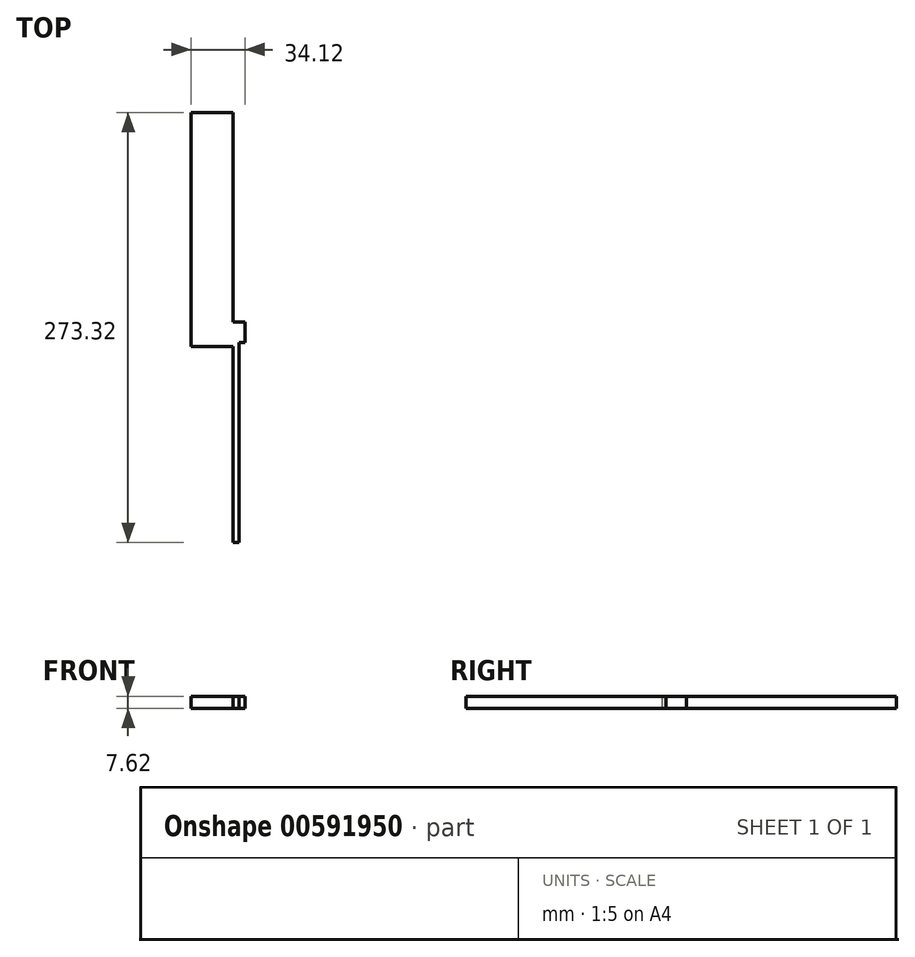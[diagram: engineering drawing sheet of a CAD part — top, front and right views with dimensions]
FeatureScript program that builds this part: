
annotation { "Feature Type Name" : "Feature", "Feature Type Description" : "" }
export const myFeature = defineFeature(function(context is Context, id is Id, definition is map)
    precondition{}
    {
        {
            var Q0;
            Q0=qCreatedBy(makeId("Top.planeOp"),FACE);
            var sketch = newSketch(context, id + "F0", { "sketchPlane" : qUnion([Q0])});
            skLineSegment(sketch, "E0.bottom", {"start": v(-51.2, 33.08) * mm, "end": v(-24.7, 33.08) * mm});
            skLineSegment(sketch, "E0.top", {"start": v(-51.2, -115.79) * mm, "end": v(-24.7, -115.79) * mm});
            skLineSegment(sketch, "E0.left", {"start": v(-51.2, 33.08) * mm, "end": v(-51.2, -115.79) * mm});
            skLineSegment(sketch, "E0.right", {"start": v(-24.7, 33.08) * mm, "end": v(-24.7, -115.79) * mm});
            skSolve(sketch);
        }
        {
            var Q0;
            Q0=makeQuery(id+"F0.imprint","IMPRINT",FACE,{"disambiguationData":[TD([[makeQuery(id+"F0.imprint","IMPRINT",EDGE,{"derivedFrom":sQuery(id+"F0.wireOp",EDGE,"E0.bottom")}),-1.0]])]});
            extrude(context, id + "F1", {"entities" : qUnion([Q0]), "depth" : 7.62 * mm, "offsetDistance" : 25.4 * mm});
        }
        {
            var Q0;
            Q0=makeQuery(id+"F1.opExtrude","SWEPT_FACE",FACE,{"disambiguationData":[OSD([sQuery(id+"F0.wireOp",EDGE,"E0.right")])]});
            var sketch = newSketch(context, id + "F2", { "sketchPlane" : qUnion([Q0])});
            skLineSegment(sketch, "E1.bottom", {"start": v(-100.23, 7.62) * mm, "end": v(-113.24, 7.62) * mm});
            skLineSegment(sketch, "E1.top", {"start": v(-100.23, 0) * mm, "end": v(-113.24, 0) * mm});
            skLineSegment(sketch, "E1.left", {"start": v(-100.23, 7.62) * mm, "end": v(-100.23, 0) * mm});
            skLineSegment(sketch, "E1.right", {"start": v(-113.24, 7.62) * mm, "end": v(-113.24, 0) * mm});
            skSolve(sketch);
        }
        {
            var Q0;
            Q0 = qSketchRegion(id + "F2", true);
            extrude(context, id + "F3", {"entities" : qUnion([Q0]), "operationType" : NewBodyOperationType.ADD, "depth" : 7.62 * mm, "offsetDistance" : 25.4 * mm});
        }
        {
            var Q0;
            Q0=makeQuery(id+"F3.opExtrude","SWEPT_FACE",FACE,{"disambiguationData":[OSD([sQuery(id+"F2.wireOp",EDGE,"E1.right")])]});
            var sketch = newSketch(context, id + "F4", { "sketchPlane" : qUnion([Q0])});
            skLineSegment(sketch, "E2.bottom", {"start": v(-20.9, 7.62) * mm, "end": v(-24.7, 7.62) * mm});
            skLineSegment(sketch, "E2.top", {"start": v(-20.9, 0) * mm, "end": v(-24.7, 0) * mm});
            skLineSegment(sketch, "E2.left", {"start": v(-20.9, 7.62) * mm, "end": v(-20.9, 0) * mm});
            skLineSegment(sketch, "E2.right", {"start": v(-24.7, 7.62) * mm, "end": v(-24.7, 0) * mm});
            skSolve(sketch);
        }
        {
            var Q0;
            Q0 = qSketchRegion(id + "F4", true);
            extrude(context, id + "F5", {"entities" : qUnion([Q0]), "operationType" : NewBodyOperationType.ADD, "depth" : 127 * mm, "offsetDistance" : 25.4 * mm});
        }
    });
